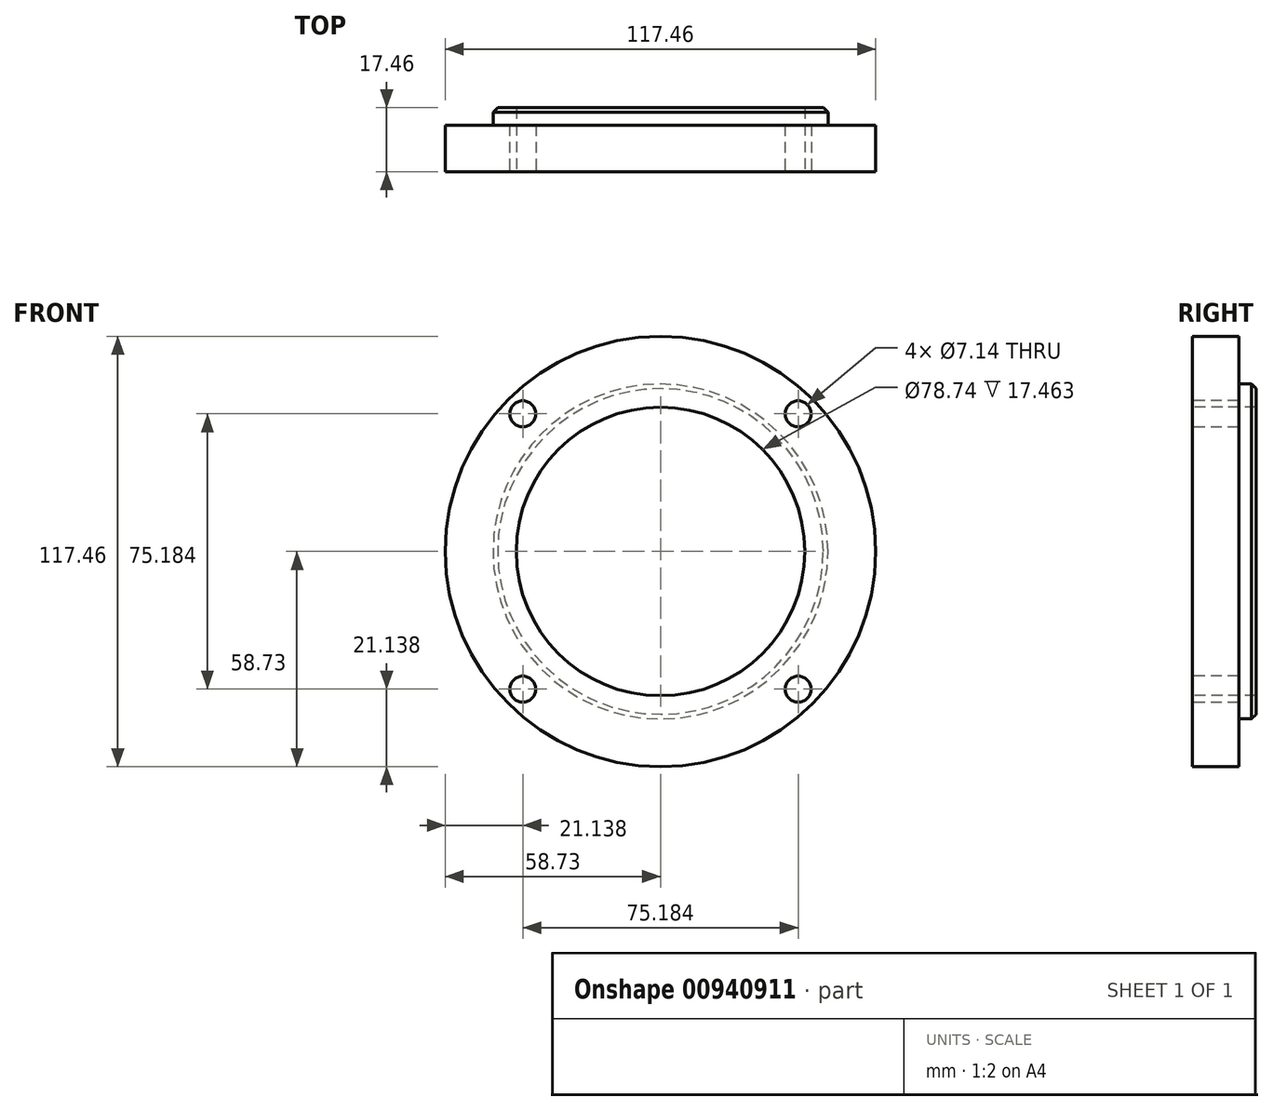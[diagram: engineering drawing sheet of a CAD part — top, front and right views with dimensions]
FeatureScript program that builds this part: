
annotation { "Feature Type Name" : "Feature", "Feature Type Description" : "" }
export const myFeature = defineFeature(function(context is Context, id is Id, definition is map)
    precondition{}
    {
        {
            var Q0;
            Q0=qCreatedBy(makeId("Front.planeOp"),FACE);
            var sketch = newSketch(context, id + "F0", { "sketchPlane" : qUnion([Q0])});
            skCircle(sketch, "E0", {"center": v(0, 0) * mm, "radius": 58.73 * mm});
            skSolve(sketch);
        }
        {
            var Q0;
            Q0=makeQuery(id+"F0.imprint","IMPRINT",FACE,{"disambiguationData":[TD([[makeQuery(id+"F0.imprint","IMPRINT",EDGE,{"derivedFrom":sQuery(id+"F0.wireOp",EDGE,"E0")}),1.0]])]});
            extrude(context, id + "F1", {"entities" : qUnion([Q0]), "depth" : 17.46 * mm, "offsetDistance" : 25.4 * mm});
        }
        {
            var Q0;
            Q0=qCreatedBy(makeId("Top.planeOp"),FACE);
            var sketch = newSketch(context, id + "F2", { "sketchPlane" : qUnion([Q0])});
            skLineSegment(sketch, "E1.bottom", {"start": v(-63.35, 3.35) * mm, "end": v(-45.72, 3.35) * mm});
            skLineSegment(sketch, "E1.top", {"start": v(-63.35, -4.75) * mm, "end": v(-45.72, -4.75) * mm});
            skLineSegment(sketch, "E1.left", {"start": v(-63.35, 3.35) * mm, "end": v(-63.35, -4.75) * mm});
            skLineSegment(sketch, "E1.right", {"start": v(-45.72, 3.35) * mm, "end": v(-45.72, -4.75) * mm});
            skLineSegment(sketch, "E2", {"start": v(0, 24.74) * mm, "end": v(0, -28.35) * mm});
            skSolve(sketch);
        }
        {
            var Q0;
            Q0=makeQuery(id+"F2.imprint","IMPRINT",FACE,{"disambiguationData":[TD([[makeQuery(id+"F2.imprint","IMPRINT",EDGE,{"derivedFrom":sQuery(id+"F2.wireOp",EDGE,"E1.bottom")}),-1.0]])]});
            var Q1;
            Q1=sQuery(id+"F2.wireOp",EDGE,"E2");
            revolve(context, id + "F3", {"operationType" : NewBodyOperationType.REMOVE, "surfaceOperationType" : NewSurfaceOperationType.NEW, "entities" : qUnion([Q0]), "axis" : qUnion([Q1]), "revolveType" : RevolveType.FULL, "oppositeDirection" : true});
        }
        {
            var Q0;
            Q0=makeQuery(id+"F3.boolean.opBoolean","INTERSECT",EDGE,{"derivedFrom":[makeQuery(id+"F1.opExtrude","CAP_FACE",FACE,{"disambiguationData":[OSD([sQuery(id+"F0.wireOp",EDGE,"E0")])],"isStart":true}),makeQuery(id+"F3.opRevolve","SWEPT_FACE",FACE,{"disambiguationData":[OSD([sQuery(id+"F2.wireOp",EDGE,"E1.right")])]})]});
            chamfer(context, id + "F4", {"entities" : qUnion([Q0]), "width" : 1.27 * mm, "tangentPropagation" : true});
        }
        {
            var Q0;
            Q0=makeQuery(id+"F1.opExtrude","CAP_FACE",FACE,{"disambiguationData":[OSD([sQuery(id+"F0.wireOp",EDGE,"E0")])],"isStart":false});
            var sketch = newSketch(context, id + "F5", { "sketchPlane" : qUnion([Q0])});
            skPoint(sketch, "E3", {"position": v(-37.6, 37.6) * mm});
            skPoint(sketch, "E4", {"position": v(37.6, 37.6) * mm});
            skPoint(sketch, "E5", {"position": v(37.6, -37.6) * mm});
            skPoint(sketch, "E6", {"position": v(-37.6, -37.6) * mm});
            skPoint(sketch, "E7", {"position": v(0, 0) * mm});
            skSolve(sketch);
        }
        {
            var Q0;
            Q0=sQuery(id+"F5.wireOp",VERTEX,"E3");
            var Q1;
            Q1=sQuery(id+"F5.wireOp",VERTEX,"E4");
            var Q2;
            Q2=sQuery(id+"F5.wireOp",VERTEX,"E5");
            var Q3;
            Q3=sQuery(id+"F5.wireOp",VERTEX,"E6");
            var Q4;
            Q4=makeQuery(id+"F1.opExtrude","SWEPT_BODY",BODY,{"disambiguationData":[OSD([sQuery(id+"F0.wireOp",EDGE,"E0")])]});
            hole(context, id + "F6", {"style" : HoleStyle.SIMPLE, "endStyle" : HoleEndStyle.THROUGH, "standardTappedOrClearance" : lookupTablePath({ "fit" : "Normal (ASME)", "standard" : "ANSI", "size" : "1/4", "type" : "Clearance" }), "standardBlindInLast" : lookupTablePath({ "fit" : "Normal", "standard" : "ANSI", "engagement" : "75%", "pitch" : "20 tpi", "size" : "1/4", "type" : "Clearance & tapped" }), "holeDiameter" : 7.14 * mm, "majorDiameter" : 3.5 * mm, "isTappedThrough" : true, "tappedDepth" : 5.56 * mm, "tapClearance" : 3, "locations" : qUnion([Q0, Q1, Q2, Q3]), "scope" : qUnion([Q4])});
        }
        {
            var Q0;
            Q0=sQuery(id+"F5.wireOp",VERTEX,"E7");
            var Q1;
            Q1=makeQuery(id+"F1.opExtrude","SWEPT_BODY",BODY,{"disambiguationData":[OSD([sQuery(id+"F0.wireOp",EDGE,"E0")])]});
            hole(context, id + "F7", {"style" : HoleStyle.SIMPLE, "endStyle" : HoleEndStyle.THROUGH, "holeDiameter" : 78.74 * mm, "majorDiameter" : 6.35 * mm, "isTappedThrough" : true, "tappedDepth" : 5.56 * mm, "tapClearance" : 3, "locations" : qUnion([Q0]), "scope" : qUnion([Q1])});
        }
    });
